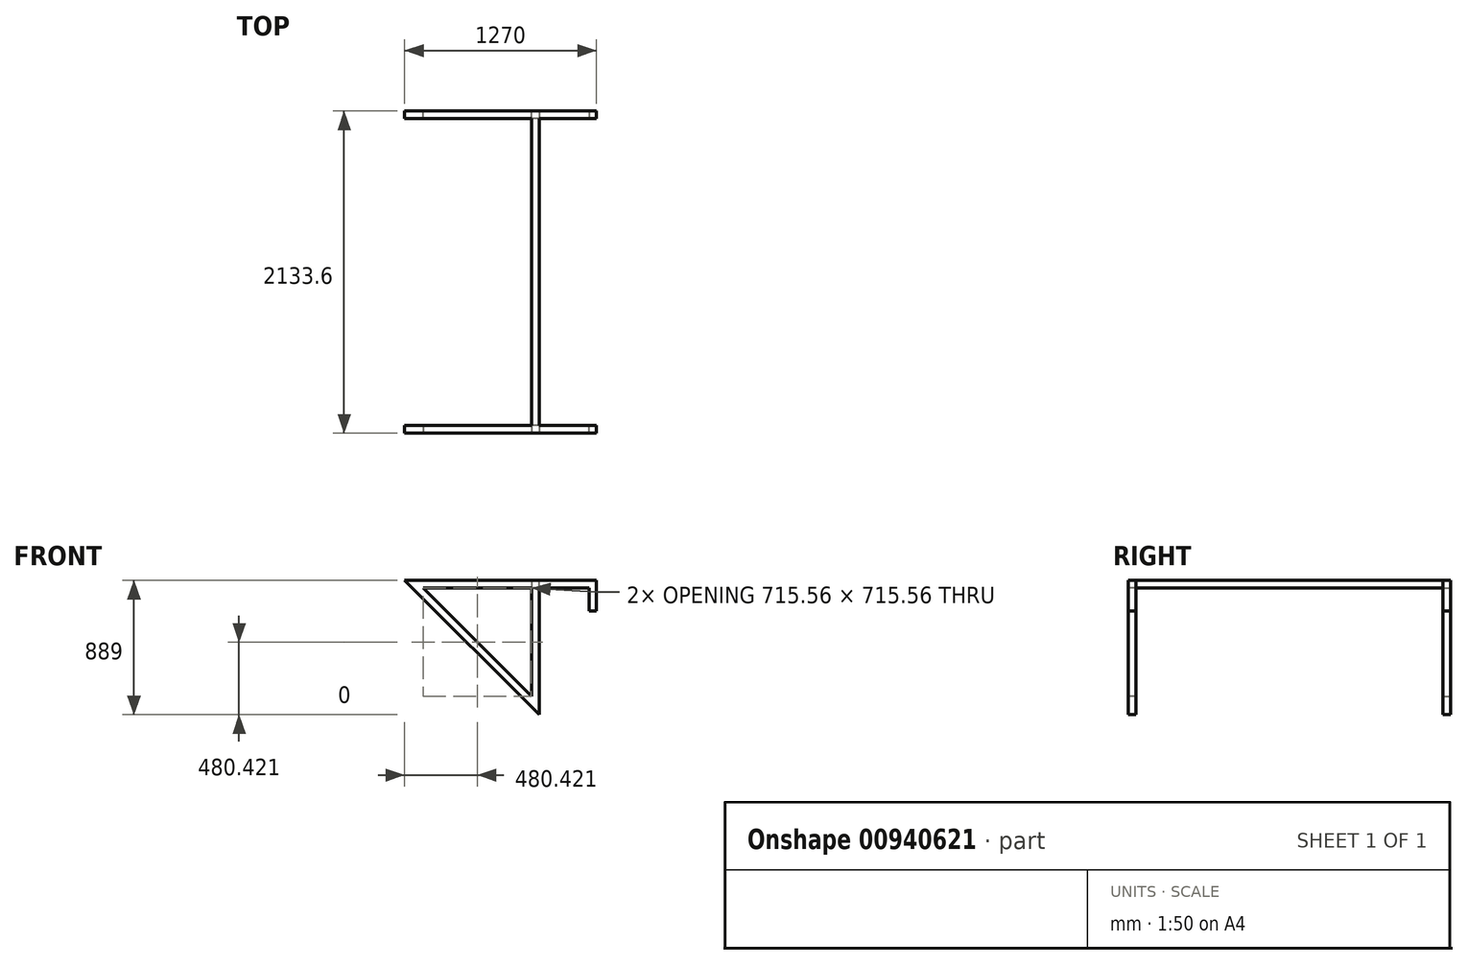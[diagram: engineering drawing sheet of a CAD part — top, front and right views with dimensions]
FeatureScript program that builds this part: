
annotation { "Feature Type Name" : "Feature", "Feature Type Description" : "" }
export const myFeature = defineFeature(function(context is Context, id is Id, definition is map)
    precondition{}
    {
        {
            var Q0;
            Q0=qCreatedBy(makeId("Front.planeOp"),FACE);
            var sketch = newSketch(context, id + "F0", { "sketchPlane" : qUnion([Q0])});
            skLineSegment(sketch, "E0", {"start": v(-203.2, 50.8) * mm, "end": v(685.8, 50.8) * mm});
            skLineSegment(sketch, "E1", {"start": v(685.8, 50.8) * mm, "end": v(685.8, -838.2) * mm});
            skLineSegment(sketch, "E2", {"start": v(-203.2, 50.8) * mm, "end": v(685.8, -838.2) * mm});
            skSolve(sketch);
        }
        {
            var Q0;
            Q0=makeQuery(id+"F0.imprint","IMPRINT",FACE,{"disambiguationData":[TD([[makeQuery(id+"F0.imprint","IMPRINT",EDGE,{"derivedFrom":sQuery(id+"F0.wireOp",EDGE,"E0")}),-1.0]])]});
            extrude(context, id + "F1", {"entities" : qUnion([Q0]), "depth" : 50.8 * mm, "offsetDistance" : 25.4 * mm});
        }
        {
            var Q0;
            Q0=makeQuery(id+"F1.opExtrude","CAP_FACE",FACE,{"disambiguationData":[OSD([sQuery(id+"F0.wireOp",EDGE,"E0"),sQuery(id+"F0.wireOp",EDGE,"E1"),sQuery(id+"F0.wireOp",EDGE,"E2")])],"isStart":true});
            var sketch = newSketch(context, id + "F2", { "sketchPlane" : qUnion([Q0])});
            skLineSegment(sketch, "E3.bottom", {"start": v(-685.8, 50.8) * mm, "end": v(-635, 50.8) * mm});
            skLineSegment(sketch, "E3.top", {"start": v(-685.8, 0) * mm, "end": v(-635, 0) * mm});
            skLineSegment(sketch, "E3.left", {"start": v(-685.8, 50.8) * mm, "end": v(-685.8, 0) * mm});
            skLineSegment(sketch, "E3.right", {"start": v(-635, 50.8) * mm, "end": v(-635, 0) * mm});
            skSolve(sketch);
        }
        {
            var Q0;
            Q0 = qSketchRegion(id + "F2", true);
            extrude(context, id + "F3", {"entities" : qUnion([Q0]), "operationType" : NewBodyOperationType.ADD, "depth" : 1016 * mm, "offsetDistance" : 25.4 * mm});
        }
        {
            var Q0;
            Q0=makeQuery(id+"F0.imprint","IMPRINT",FACE,{"disambiguationData":[TD([[makeQuery(id+"F0.imprint","IMPRINT",EDGE,{"derivedFrom":sQuery(id+"F0.wireOp",EDGE,"E0")}),-1.0]])]});
            var sketch = newSketch(context, id + "F4", { "sketchPlane" : qUnion([Q0])});
            skLineSegment(sketch, "E4", {"start": v(685.8, -838.2) * mm, "end": v(649.79, -802.37) * mm});
            skLineSegment(sketch, "E5", {"start": v(649.79, -802.37) * mm, "end": v(685.8, -838.2) * mm});
            skLineSegment(sketch, "E6", {"start": v(685.8, -787.4) * mm, "end": v(685.8, -838.2) * mm});
            skLineSegment(sketch, "E7", {"start": v(685.8, -787.4) * mm, "end": v(649.79, -802.37) * mm});
            skSolve(sketch);
        }
        {
            var Q0;
            Q0=makeQuery(id+"FVzkL5AV8VG29R1_1.boolean.opBoolean","MERGE",FACE,{"derivedFrom":[makeQuery(id+"F3.boolean.opBoolean","MERGE",FACE,{"derivedFrom":[makeQuery(id+"F1.opExtrude","SWEPT_FACE",FACE,{"disambiguationData":[OSD([sQuery(id+"F0.wireOp",EDGE,"E1")])]}),makeQuery(id+"F3.opExtrude","SWEPT_FACE",FACE,{"disambiguationData":[OSD([sQuery(id+"F2.wireOp",EDGE,"E3.left")])]})]}),makeQuery(id+"FVzkL5AV8VG29R1_1.opExtrude","SWEPT_FACE",FACE,{"disambiguationData":[OSD([sQuery(id+"F4.wireOp",EDGE,"E6")])]})]});
            var sketch = newSketch(context, id + "F5", { "sketchPlane" : qUnion([Q0])});
            skLineSegment(sketch, "E8.bottom", {"start": v(0, 0) * mm, "end": v(-50.8, 0) * mm});
            skLineSegment(sketch, "E8.top", {"start": v(0, 50.8) * mm, "end": v(-50.8, 50.8) * mm});
            skLineSegment(sketch, "E8.left", {"start": v(0, 0) * mm, "end": v(0, 50.8) * mm});
            skLineSegment(sketch, "E8.right", {"start": v(-50.8, 0) * mm, "end": v(-50.8, 50.8) * mm});
            skSolve(sketch);
        }
        {
            var Q0;
            Q0=makeQuery(id+"F5.imprint","IMPRINT",FACE,{"disambiguationData":[TD([[makeQuery(id+"F5.imprint","IMPRINT",EDGE,{"derivedFrom":sQuery(id+"F5.wireOp",EDGE,"E8.bottom")}),-1.0]])]});
            extrude(context, id + "F6", {"entities" : qUnion([Q0]), "operationType" : NewBodyOperationType.ADD, "depth" : 381 * mm, "offsetDistance" : 25.4 * mm});
        }
        {
            var Q0;
            {var subQ0=sQuery(id+"F4.wireOp",EDGE,"E6");var subQ1=makeQuery(id+"FVzkL5AV8VG29R1_1.opExtrude","SWEPT_FACE",FACE,{"disambiguationData":[OSD([subQ0])]});var subQ4=makeQuery(id+"F3.opExtrude","SWEPT_FACE",FACE,{"disambiguationData":[OSD([sQuery(id+"F2.wireOp",EDGE,"E3.left")])]});var subQ5=sQuery(id+"F0.wireOp",EDGE,"E2");var subQ6=sQuery(id+"F0.wireOp",EDGE,"E1");var subQ8=makeQuery(id+"F1.opExtrude","SWEPT_FACE",FACE,{"disambiguationData":[OSD([subQ6])]});Q0=makeQuery(id+"F6.boolean.opBoolean","SPLIT",FACE,{"disambiguationData":[TD([makeQuery(id+"F1.opExtrude","SWEPT_FACE",FACE,{"disambiguationData":[OSD([subQ5])]})])],"derivedFrom":makeQuery(id+"FVzkL5AV8VG29R1_1.boolean.opBoolean","MERGE",FACE,{"derivedFrom":[makeQuery(id+"F3.boolean.opBoolean","MERGE",FACE,{"derivedFrom":[subQ8,subQ4]}),subQ1]})});}
            var sketch = newSketch(context, id + "F7", { "sketchPlane" : qUnion([Q0])});
            skLineSegment(sketch, "E9.bottom", {"start": v(-50.8, -838.2) * mm, "end": v(25.4, -838.2) * mm});
            skLineSegment(sketch, "E9.top", {"start": v(-50.8, -787.4) * mm, "end": v(25.4, -787.4) * mm});
            skLineSegment(sketch, "E9.left", {"start": v(-50.8, -838.2) * mm, "end": v(-50.8, -787.4) * mm});
            skLineSegment(sketch, "E9.right", {"start": v(25.4, -838.2) * mm, "end": v(25.4, -787.4) * mm});
            skSolve(sketch);
        }
        {
            var Q0;
            Q0=makeQuery(id+"Fc25ocHKRKDElpb_1.boolean.opBoolean","MERGE",FACE,{"derivedFrom":[makeQuery(id+"F6.boolean.opBoolean","MERGE",FACE,{"derivedFrom":[makeQuery(id+"F1.opExtrude","CAP_FACE",FACE,{"disambiguationData":[OSD([sQuery(id+"F0.wireOp",EDGE,"E0"),sQuery(id+"F0.wireOp",EDGE,"E1"),sQuery(id+"F0.wireOp",EDGE,"E2")])],"isStart":false}),makeQuery(id+"F6.opExtrude","SWEPT_FACE",FACE,{"disambiguationData":[OSD([sQuery(id+"F5.wireOp",EDGE,"E8.right")])]})]}),makeQuery(id+"Fc25ocHKRKDElpb_1.opExtrude","SWEPT_FACE",FACE,{"disambiguationData":[OSD([sQuery(id+"F7.wireOp",EDGE,"E9.left")])]})]});
            var sketch = newSketch(context, id + "F8", { "sketchPlane" : qUnion([Q0])});
            skLineSegment(sketch, "E10", {"start": v(635, 0) * mm, "end": v(-80.56, 0) * mm});
            skLineSegment(sketch, "E11", {"start": v(635, 0) * mm, "end": v(635, -715.56) * mm});
            skLineSegment(sketch, "E12", {"start": v(-80.56, 0) * mm, "end": v(635, -715.56) * mm});
            skSolve(sketch);
        }
        {
            var Q0;
            Q0=makeQuery(id+"F8.imprint","IMPRINT",FACE,{"disambiguationData":[TD([[makeQuery(id+"F8.imprint","IMPRINT",EDGE,{"derivedFrom":sQuery(id+"F8.wireOp",EDGE,"E10")}),1.0]])]});
            extrude(context, id + "F9", {"entities" : qUnion([Q0]), "operationType" : NewBodyOperationType.REMOVE, "endBound" : BoundingType.THROUGH_ALL, "oppositeDirection" : true, "depth" : 25.4 * mm, "offsetDistance" : 25.4 * mm});
        }
        {
            var Q0;
            Q0=makeQuery(id+"F3.opExtrude","CAP_FACE",FACE,{"disambiguationData":[OSD([sQuery(id+"F2.wireOp",EDGE,"E3.bottom"),sQuery(id+"F2.wireOp",EDGE,"E3.top"),sQuery(id+"F2.wireOp",EDGE,"E3.left"),sQuery(id+"F2.wireOp",EDGE,"E3.right")])],"isStart":false});
            var Q1;
            Q1=makeQuery(id+"F3.opExtrude","CAP_VERTEX",VERTEX,{"disambiguationData":[OSD([sQuery(id+"F0.wireOp",EDGE,"E1"),sQuery(id+"F2.wireOp",EDGE,"E3.top"),sQuery(id+"F2.wireOp",EDGE,"E3.left")])],"isStart":false});
            cPlane(context, id + "F10", {"entities" : qUnion([Q0, Q1]), "cplaneType" : CPlaneType.PLANE_POINT, "offset" : 25.4 * mm, "width" : 152.4 * mm, "height" : 152.4 * mm});
        }
        {
            var Q0;
            Q0=makeQuery(id+"F6.opExtrude","SWEPT_FACE",FACE,{"disambiguationData":[OSD([sQuery(id+"F5.wireOp",EDGE,"E8.bottom")])]});
            var sketch = newSketch(context, id + "F11", { "sketchPlane" : qUnion([Q0])});
            skLineSegment(sketch, "E13.bottom", {"start": v(1066.8, 50.8) * mm, "end": v(1016, 50.8) * mm});
            skLineSegment(sketch, "E13.top", {"start": v(1066.8, 0) * mm, "end": v(1016, 0) * mm});
            skLineSegment(sketch, "E13.left", {"start": v(1066.8, 50.8) * mm, "end": v(1066.8, 0) * mm});
            skLineSegment(sketch, "E13.right", {"start": v(1016, 50.8) * mm, "end": v(1016, 0) * mm});
            skSolve(sketch);
        }
        {
            var Q0;
            Q0=makeQuery(id+"F11.imprint","IMPRINT",FACE,{"disambiguationData":[TD([[makeQuery(id+"F11.imprint","IMPRINT",EDGE,{"derivedFrom":sQuery(id+"F11.wireOp",EDGE,"E13.bottom")}),1.0]])]});
            extrude(context, id + "F12", {"entities" : qUnion([Q0]), "operationType" : NewBodyOperationType.ADD, "depth" : 152.4 * mm, "offsetDistance" : 25.4 * mm});
        }
        {
            var Q0;
            Q0=makeQuery(id+"F1.opExtrude","SWEPT_BODY",BODY,{"disambiguationData":[OSD([sQuery(id+"F0.wireOp",EDGE,"E0"),sQuery(id+"F0.wireOp",EDGE,"E1"),sQuery(id+"F0.wireOp",EDGE,"E2")])]});
            var Q1;
            Q1=qCreatedBy(id+"F10.planeOp",FACE);
            mirror(context, id + "F13", {"operationType" : NewBodyOperationType.ADD, "entities" : qUnion([Q0]), "mirrorPlane" : qUnion([Q1])});
        }
    });
